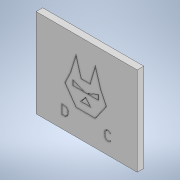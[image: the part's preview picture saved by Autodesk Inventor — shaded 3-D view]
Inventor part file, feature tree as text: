
AUTODESK INVENTOR PART (.ipt)
format: ipt  version: 2022 (Build 260153000, 153)  size: 207,872 bytes
history: native  units: in
note: dims shown in document units (in); Inventor stores cm internally (conversion verified against a paired STEP export)
features: extrude x2, sketch x2
ambient origin geometry x8: Origin, YZ Plane, XZ Plane, XY Plane, X Axis, Y Axis, Z Axis, Center Point
bodies: Solid1 (feature_tree)
feature tree (4):
  extrude  "Extrusion1"  Depth=10.6299in
  extrude  "Extrusion2"  Depth=0.0591in
  sketch  "Sketch1"  dims[d0=12.126in d1=10.6299in]
  sketch  "Sketch2"  dims[d2=0.7874in d3=0.0in d5=0.0591in d6=0.0591in d7=0.0591in d8=0.0591in d9=0.315in d10=0.0in]
